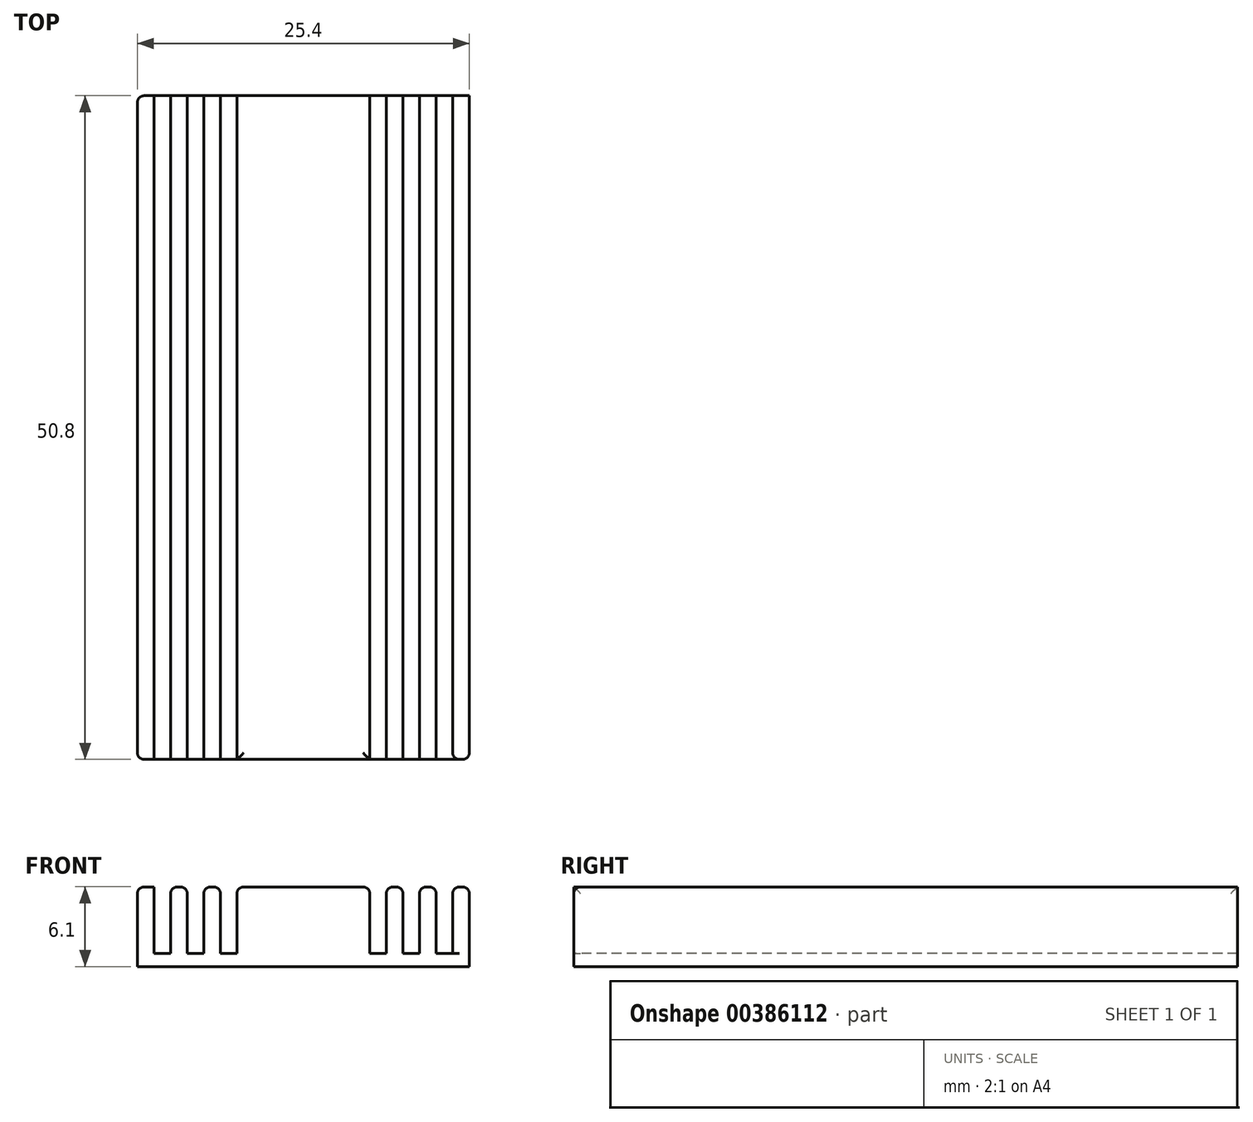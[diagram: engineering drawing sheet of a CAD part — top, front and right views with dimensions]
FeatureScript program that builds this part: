
annotation { "Feature Type Name" : "Feature", "Feature Type Description" : "" }
export const myFeature = defineFeature(function(context is Context, id is Id, definition is map)
    precondition{}
    {
        {
            var Q0;
            Q0=qCreatedBy(makeId("Top.planeOp"),FACE);
            var sketch = newSketch(context, id + "F0", { "sketchPlane" : qUnion([Q0])});
            skLineSegment(sketch, "E0.bottom", {"start": v(12.7, 25.4) * mm, "end": v(-12.7, 25.4) * mm});
            skLineSegment(sketch, "E0.top", {"start": v(12.7, -25.4) * mm, "end": v(-12.7, -25.4) * mm});
            skLineSegment(sketch, "E0.left", {"start": v(12.7, 25.4) * mm, "end": v(12.7, -25.4) * mm});
            skLineSegment(sketch, "E0.right", {"start": v(-12.7, 25.4) * mm, "end": v(-12.7, -25.4) * mm});
            skPoint(sketch, "E0.middle", {"position": v(0, 0) * mm});
            skSolve(sketch);
        }
        {
            var Q0;
            Q0=makeQuery(id+"F0.imprint","IMPRINT",FACE,{"disambiguationData":[TD([[makeQuery(id+"F0.imprint","IMPRINT",EDGE,{"derivedFrom":sQuery(id+"F0.wireOp",EDGE,"E0.bottom")}),1.0]])]});
            extrude(context, id + "F1", {"entities" : qUnion([Q0]), "depth" : 6.1 * mm});
        }
        {
            var Q0;
            Q0=makeQuery(id+"F1.opExtrude","SWEPT_FACE",FACE,{"disambiguationData":[OSD([sQuery(id+"F0.wireOp",EDGE,"E0.top")])]});
            var sketch = newSketch(context, id + "F2", { "sketchPlane" : qUnion([Q0])});
            skLineSegment(sketch, "E1.0", {"start": v(-12.7, 6.1) * mm, "end": v(-12.7, 0) * mm});
            skLineSegment(sketch, "E2.0", {"start": v(12.7, 6.1) * mm, "end": v(-12.7, 6.1) * mm});
            skLineSegment(sketch, "E3.0", {"start": v(12.7, 6.1) * mm, "end": v(12.7, 0) * mm});
            skLineSegment(sketch, "E4", {"start": v(-12.7, 6.1) * mm, "end": v(-11.43, 6.1) * mm});
            skLineSegment(sketch, "E5", {"start": v(-11.43, 6.1) * mm, "end": v(-11.43, 1.02) * mm});
            skLineSegment(sketch, "E6", {"start": v(-11.43, 1.02) * mm, "end": v(-10.16, 1.02) * mm});
            skLineSegment(sketch, "E7", {"start": v(-10.16, 1.02) * mm, "end": v(-10.16, 6.1) * mm});
            skLineSegment(sketch, "E8", {"start": v(-10.16, 6.1) * mm, "end": v(-8.9, 6.1) * mm});
            skLineSegment(sketch, "E9", {"start": v(-8.9, 6.1) * mm, "end": v(-8.9, 1.02) * mm});
            skLineSegment(sketch, "E10", {"start": v(-8.9, 1.02) * mm, "end": v(-7.62, 1.02) * mm});
            skLineSegment(sketch, "E11", {"start": v(-7.62, 1.02) * mm, "end": v(-7.62, 6.1) * mm});
            skLineSegment(sketch, "E12", {"start": v(-7.62, 6.1) * mm, "end": v(-6.35, 6.1) * mm});
            skLineSegment(sketch, "E13", {"start": v(-6.35, 6.1) * mm, "end": v(-6.35, 1.02) * mm});
            skLineSegment(sketch, "E14", {"start": v(-6.35, 1.02) * mm, "end": v(-5.08, 1.02) * mm});
            skLineSegment(sketch, "E15", {"start": v(-5.08, 1.02) * mm, "end": v(-5.08, 6.1) * mm});
            skLineSegment(sketch, "E16", {"start": v(-5.08, 6.1) * mm, "end": v(5.08, 6.1) * mm});
            skLineSegment(sketch, "E17", {"start": v(5.08, 6.1) * mm, "end": v(5.08, 1.02) * mm});
            skLineSegment(sketch, "E18", {"start": v(5.08, 1.02) * mm, "end": v(6.35, 1.02) * mm});
            skLineSegment(sketch, "E19", {"start": v(6.35, 1.02) * mm, "end": v(6.35, 6.1) * mm});
            skLineSegment(sketch, "E20", {"start": v(6.35, 6.1) * mm, "end": v(7.62, 6.1) * mm});
            skLineSegment(sketch, "E21", {"start": v(7.62, 6.1) * mm, "end": v(7.62, 1.02) * mm});
            skLineSegment(sketch, "E22", {"start": v(7.62, 1.02) * mm, "end": v(8.9, 1.02) * mm});
            skLineSegment(sketch, "E23", {"start": v(8.9, 1.02) * mm, "end": v(8.9, 6.1) * mm});
            skLineSegment(sketch, "E24", {"start": v(8.9, 6.1) * mm, "end": v(10.16, 6.1) * mm});
            skLineSegment(sketch, "E25", {"start": v(10.16, 6.1) * mm, "end": v(10.16, 1.02) * mm});
            skLineSegment(sketch, "E26", {"start": v(10.16, 1.02) * mm, "end": v(11.43, 1.02) * mm});
            skLineSegment(sketch, "E27", {"start": v(11.43, 1.02) * mm, "end": v(11.43, 6.1) * mm});
            skLineSegment(sketch, "E28", {"start": v(11.43, 6.1) * mm, "end": v(12.7, 6.1) * mm});
            skSolve(sketch);
        }
        {
            var Q0;
            {var subQ0=sQuery(id+"F2.wireOp",EDGE,"E5");Q0=makeQuery(id+"F2.imprint","IMPRINT",FACE,{"disambiguationData":[TD([[makeQuery(id+"F2.imprint","IMPRINT",EDGE,{"derivedFrom":subQ0}),1.0]])]});}
            var Q1;
            {var subQ0=sQuery(id+"F2.wireOp",EDGE,"E9");Q1=makeQuery(id+"F2.imprint","IMPRINT",FACE,{"disambiguationData":[TD([[makeQuery(id+"F2.imprint","IMPRINT",EDGE,{"derivedFrom":subQ0}),1.0]])]});}
            var Q2;
            {var subQ0=sQuery(id+"F2.wireOp",EDGE,"E13");Q2=makeQuery(id+"F2.imprint","IMPRINT",FACE,{"disambiguationData":[TD([[makeQuery(id+"F2.imprint","IMPRINT",EDGE,{"derivedFrom":subQ0}),1.0]])]});}
            var Q3;
            {var subQ0=sQuery(id+"F2.wireOp",EDGE,"E17");Q3=makeQuery(id+"F2.imprint","IMPRINT",FACE,{"disambiguationData":[TD([[makeQuery(id+"F2.imprint","IMPRINT",EDGE,{"derivedFrom":subQ0}),1.0]])]});}
            var Q4;
            {var subQ0=sQuery(id+"F2.wireOp",EDGE,"E21");Q4=makeQuery(id+"F2.imprint","IMPRINT",FACE,{"disambiguationData":[TD([[makeQuery(id+"F2.imprint","IMPRINT",EDGE,{"derivedFrom":subQ0}),1.0]])]});}
            var Q5;
            {var subQ2=sQuery(id+"F2.wireOp",EDGE,"E25");Q5=makeQuery(id+"F2.imprint","IMPRINT",FACE,{"disambiguationData":[TD([[makeQuery(id+"F2.imprint","IMPRINT",EDGE,{"derivedFrom":subQ2}),1.0]])]});}
            extrude(context, id + "F3", {"entities" : qUnion([Q0, Q1, Q2, Q3, Q4, Q5]), "operationType" : NewBodyOperationType.REMOVE, "oppositeDirection" : true, "depth" : 50.8 * mm});
        }
        {
            var Q0;
            Q0=makeQuery(id+"F3.boolean.opBoolean","COPY",EDGE,{"derivedFrom":makeQuery(id+"F3.opExtrude","SWEPT_EDGE",EDGE,{"disambiguationData":[OSD([sQuery(id+"F2.wireOp",EDGE,"E2.0"),sQuery(id+"F2.wireOp",EDGE,"E4"),sQuery(id+"F2.wireOp",EDGE,"E5")])]})});
            var Q1;
            Q1=makeQuery(id+"F3.boolean.opBoolean","COPY",EDGE,{"derivedFrom":makeQuery(id+"F3.opExtrude","SWEPT_EDGE",EDGE,{"disambiguationData":[OSD([sQuery(id+"F2.wireOp",EDGE,"E2.0"),sQuery(id+"F2.wireOp",EDGE,"E7"),sQuery(id+"F2.wireOp",EDGE,"E8")])]})});
            var Q2;
            Q2=makeQuery(id+"F3.boolean.opBoolean","COPY",EDGE,{"derivedFrom":makeQuery(id+"F3.opExtrude","SWEPT_EDGE",EDGE,{"disambiguationData":[OSD([sQuery(id+"F2.wireOp",EDGE,"E2.0"),sQuery(id+"F2.wireOp",EDGE,"E8"),sQuery(id+"F2.wireOp",EDGE,"E9")])]})});
            var Q3;
            Q3=makeQuery(id+"F3.boolean.opBoolean","COPY",EDGE,{"derivedFrom":makeQuery(id+"F3.opExtrude","SWEPT_EDGE",EDGE,{"disambiguationData":[OSD([sQuery(id+"F2.wireOp",EDGE,"E2.0"),sQuery(id+"F2.wireOp",EDGE,"E11"),sQuery(id+"F2.wireOp",EDGE,"E12")])]})});
            var Q4;
            Q4=makeQuery(id+"F3.boolean.opBoolean","COPY",EDGE,{"derivedFrom":makeQuery(id+"F3.opExtrude","SWEPT_EDGE",EDGE,{"disambiguationData":[OSD([sQuery(id+"F2.wireOp",EDGE,"E2.0"),sQuery(id+"F2.wireOp",EDGE,"E12"),sQuery(id+"F2.wireOp",EDGE,"E13")])]})});
            var Q5;
            Q5=makeQuery(id+"F3.boolean.opBoolean","COPY",EDGE,{"derivedFrom":makeQuery(id+"F3.opExtrude","SWEPT_EDGE",EDGE,{"disambiguationData":[OSD([sQuery(id+"F2.wireOp",EDGE,"E2.0"),sQuery(id+"F2.wireOp",EDGE,"E15"),sQuery(id+"F2.wireOp",EDGE,"E16")])]})});
            var Q6;
            Q6=makeQuery(id+"F3.boolean.opBoolean","COPY",EDGE,{"derivedFrom":makeQuery(id+"F3.opExtrude","SWEPT_EDGE",EDGE,{"disambiguationData":[OSD([sQuery(id+"F2.wireOp",EDGE,"E2.0"),sQuery(id+"F2.wireOp",EDGE,"E16"),sQuery(id+"F2.wireOp",EDGE,"E17")])]})});
            var Q7;
            Q7=makeQuery(id+"F3.boolean.opBoolean","COPY",EDGE,{"derivedFrom":makeQuery(id+"F3.opExtrude","SWEPT_EDGE",EDGE,{"disambiguationData":[OSD([sQuery(id+"F2.wireOp",EDGE,"E2.0"),sQuery(id+"F2.wireOp",EDGE,"E19"),sQuery(id+"F2.wireOp",EDGE,"E20")])]})});
            var Q8;
            Q8=makeQuery(id+"F3.boolean.opBoolean","COPY",EDGE,{"derivedFrom":makeQuery(id+"F3.opExtrude","SWEPT_EDGE",EDGE,{"disambiguationData":[OSD([sQuery(id+"F2.wireOp",EDGE,"E2.0"),sQuery(id+"F2.wireOp",EDGE,"E20"),sQuery(id+"F2.wireOp",EDGE,"E21")])]})});
            var Q9;
            Q9=makeQuery(id+"F3.boolean.opBoolean","COPY",EDGE,{"derivedFrom":makeQuery(id+"F3.opExtrude","SWEPT_EDGE",EDGE,{"disambiguationData":[OSD([sQuery(id+"F2.wireOp",EDGE,"E2.0"),sQuery(id+"F2.wireOp",EDGE,"E23"),sQuery(id+"F2.wireOp",EDGE,"E24")])]})});
            var Q10;
            Q10=makeQuery(id+"F3.boolean.opBoolean","COPY",EDGE,{"derivedFrom":makeQuery(id+"F3.opExtrude","SWEPT_EDGE",EDGE,{"disambiguationData":[OSD([sQuery(id+"F2.wireOp",EDGE,"E2.0"),sQuery(id+"F2.wireOp",EDGE,"E24"),sQuery(id+"F2.wireOp",EDGE,"E25")])]})});
            var Q11;
            Q11=makeQuery(id+"F3.boolean.opBoolean","COPY",EDGE,{"derivedFrom":makeQuery(id+"F3.opExtrude","SWEPT_EDGE",EDGE,{"disambiguationData":[OSD([sQuery(id+"F2.wireOp",EDGE,"E2.0"),sQuery(id+"F2.wireOp",EDGE,"E27"),sQuery(id+"F2.wireOp",EDGE,"E28")])]})});
            var Q12;
            Q12=makeQuery(id+"F1.opExtrude","CAP_EDGE",EDGE,{"disambiguationData":[OSD([sQuery(id+"F0.wireOp",EDGE,"E0.left")])],"isStart":false});
            var Q13;
            {var subQ0=sQuery(id+"F0.wireOp",EDGE,"E0.top");Q13=makeQuery(id+"F3.boolean.opBoolean","SPLIT",EDGE,{"disambiguationData":[TD([makeQuery(id+"F3.opExtrude","SWEPT_FACE",FACE,{"disambiguationData":[OSD([sQuery(id+"F2.wireOp",EDGE,"E15")])]})])],"derivedFrom":makeQuery(id+"F1.opExtrude","CAP_EDGE",EDGE,{"disambiguationData":[OSD([subQ0])],"isStart":false})});}
            var Q14;
            Q14=makeQuery(id+"F3.boolean.opBoolean","COPY",EDGE,{"derivedFrom":makeQuery(id+"F3.opExtrude","CAP_EDGE",EDGE,{"disambiguationData":[OSD([sQuery(id+"F2.wireOp",EDGE,"E5")])],"isStart":true})});
            var Q15;
            Q15=makeQuery(id+"F3.boolean.opBoolean","COPY",EDGE,{"derivedFrom":makeQuery(id+"F3.opExtrude","CAP_EDGE",EDGE,{"disambiguationData":[OSD([sQuery(id+"F2.wireOp",EDGE,"E6")])],"isStart":true})});
            var Q16;
            Q16=makeQuery(id+"F3.boolean.opBoolean","COPY",EDGE,{"derivedFrom":makeQuery(id+"F3.opExtrude","CAP_EDGE",EDGE,{"disambiguationData":[OSD([sQuery(id+"F2.wireOp",EDGE,"E7")])],"isStart":true})});
            var Q17;
            Q17=makeQuery(id+"F3.boolean.opBoolean","COPY",EDGE,{"derivedFrom":makeQuery(id+"F3.opExtrude","CAP_EDGE",EDGE,{"disambiguationData":[OSD([sQuery(id+"F2.wireOp",EDGE,"E9")])],"isStart":true})});
            var Q18;
            Q18=makeQuery(id+"F3.boolean.opBoolean","COPY",EDGE,{"derivedFrom":makeQuery(id+"F3.opExtrude","CAP_EDGE",EDGE,{"disambiguationData":[OSD([sQuery(id+"F2.wireOp",EDGE,"E11")])],"isStart":true})});
            var Q19;
            Q19=makeQuery(id+"F3.boolean.opBoolean","COPY",EDGE,{"derivedFrom":makeQuery(id+"F3.opExtrude","CAP_EDGE",EDGE,{"disambiguationData":[OSD([sQuery(id+"F2.wireOp",EDGE,"E13")])],"isStart":true})});
            var Q20;
            Q20=makeQuery(id+"F3.boolean.opBoolean","COPY",EDGE,{"derivedFrom":makeQuery(id+"F3.opExtrude","CAP_EDGE",EDGE,{"disambiguationData":[OSD([sQuery(id+"F2.wireOp",EDGE,"E15")])],"isStart":true})});
            var Q21;
            Q21=makeQuery(id+"F3.boolean.opBoolean","COPY",EDGE,{"derivedFrom":makeQuery(id+"F3.opExtrude","CAP_EDGE",EDGE,{"disambiguationData":[OSD([sQuery(id+"F2.wireOp",EDGE,"E17")])],"isStart":true})});
            var Q22;
            Q22=makeQuery(id+"F3.boolean.opBoolean","COPY",EDGE,{"derivedFrom":makeQuery(id+"F3.opExtrude","CAP_EDGE",EDGE,{"disambiguationData":[OSD([sQuery(id+"F2.wireOp",EDGE,"E21")])],"isStart":true})});
            var Q23;
            Q23=makeQuery(id+"F3.boolean.opBoolean","COPY",EDGE,{"derivedFrom":makeQuery(id+"F3.opExtrude","CAP_EDGE",EDGE,{"disambiguationData":[OSD([sQuery(id+"F2.wireOp",EDGE,"E19")])],"isStart":true})});
            var Q24;
            Q24=makeQuery(id+"F3.boolean.opBoolean","COPY",EDGE,{"derivedFrom":makeQuery(id+"F3.opExtrude","CAP_EDGE",EDGE,{"disambiguationData":[OSD([sQuery(id+"F2.wireOp",EDGE,"E25")])],"isStart":true})});
            var Q25;
            Q25=makeQuery(id+"F3.boolean.opBoolean","COPY",EDGE,{"derivedFrom":makeQuery(id+"F3.opExtrude","CAP_EDGE",EDGE,{"disambiguationData":[OSD([sQuery(id+"F2.wireOp",EDGE,"E23")])],"isStart":true})});
            var Q26;
            Q26=makeQuery(id+"F3.boolean.opBoolean","COPY",EDGE,{"derivedFrom":makeQuery(id+"F3.opExtrude","CAP_EDGE",EDGE,{"disambiguationData":[OSD([sQuery(id+"F2.wireOp",EDGE,"E27")])],"isStart":true})});
            fillet(context, id + "F4", {"entities" : qUnion([Q0, Q1, Q2, Q3, Q4, Q5, Q6, Q7, Q8, Q9, Q10, Q11, Q12, Q13, Q14, Q15, Q16, Q17, Q18, Q19, Q20, Q21, Q22, Q23, Q24, Q25, Q26]), "radius" : 0.5 * mm, "tangentPropagation" : true, "allowEdgeOverflow" : false});
        }
        {
            var Q0;
            Q0=makeQuery(id+"F3.boolean.opBoolean","COPY",EDGE,{"derivedFrom":makeQuery(id+"F3.opExtrude","CAP_EDGE",EDGE,{"disambiguationData":[OSD([sQuery(id+"F2.wireOp",EDGE,"E23")])],"isStart":false})});
            var Q1;
            Q1=makeQuery(id+"F3.boolean.opBoolean","COPY",EDGE,{"derivedFrom":makeQuery(id+"F3.opExtrude","CAP_EDGE",EDGE,{"disambiguationData":[OSD([sQuery(id+"F2.wireOp",EDGE,"E21")])],"isStart":false})});
            var Q2;
            Q2=makeQuery(id+"F3.boolean.opBoolean","COPY",EDGE,{"derivedFrom":makeQuery(id+"F3.opExtrude","CAP_EDGE",EDGE,{"disambiguationData":[OSD([sQuery(id+"F2.wireOp",EDGE,"E17")])],"isStart":false})});
            var Q3;
            Q3=makeQuery(id+"F3.boolean.opBoolean","COPY",EDGE,{"derivedFrom":makeQuery(id+"F3.opExtrude","CAP_EDGE",EDGE,{"disambiguationData":[OSD([sQuery(id+"F2.wireOp",EDGE,"E11")])],"isStart":false})});
            var Q4;
            Q4=makeQuery(id+"F3.boolean.opBoolean","COPY",EDGE,{"derivedFrom":makeQuery(id+"F3.opExtrude","CAP_EDGE",EDGE,{"disambiguationData":[OSD([sQuery(id+"F2.wireOp",EDGE,"E9")])],"isStart":false})});
            var Q5;
            Q5=makeQuery(id+"F3.boolean.opBoolean","COPY",EDGE,{"derivedFrom":makeQuery(id+"F3.opExtrude","CAP_EDGE",EDGE,{"disambiguationData":[OSD([sQuery(id+"F2.wireOp",EDGE,"E5")])],"isStart":false})});
            var Q6;
            Q6=makeQuery(id+"F3.boolean.opBoolean","COPY",EDGE,{"derivedFrom":makeQuery(id+"F3.opExtrude","CAP_EDGE",EDGE,{"disambiguationData":[OSD([sQuery(id+"F2.wireOp",EDGE,"E27")])],"isStart":false})});
            var Q7;
            Q7=makeQuery(id+"F1.opExtrude","SWEPT_EDGE",EDGE,{"disambiguationData":[OSD([sQuery(id+"F0.wireOp",EDGE,"E0.bottom"),sQuery(id+"F0.wireOp",EDGE,"E0.right")])]});
            var Q8;
            Q8=makeQuery(id+"F1.opExtrude","CAP_EDGE",EDGE,{"disambiguationData":[OSD([sQuery(id+"F0.wireOp",EDGE,"E0.right")])],"isStart":false});
            var Q9;
            Q9=makeQuery(id+"F1.opExtrude","SWEPT_EDGE",EDGE,{"disambiguationData":[OSD([sQuery(id+"F0.wireOp",EDGE,"E0.top"),sQuery(id+"F0.wireOp",EDGE,"E0.right")])]});
            var Q10;
            Q10=makeQuery(id+"F1.opExtrude","SWEPT_EDGE",EDGE,{"disambiguationData":[OSD([sQuery(id+"F0.wireOp",EDGE,"E0.top"),sQuery(id+"F0.wireOp",EDGE,"E0.left")])]});
            fillet(context, id + "F5", {"entities" : qUnion([Q0, Q1, Q2, Q3, Q4, Q5, Q6, Q7, Q8, Q9, Q10]), "radius" : 0.5 * mm, "tangentPropagation" : true, "allowEdgeOverflow" : false});
        }
    });
